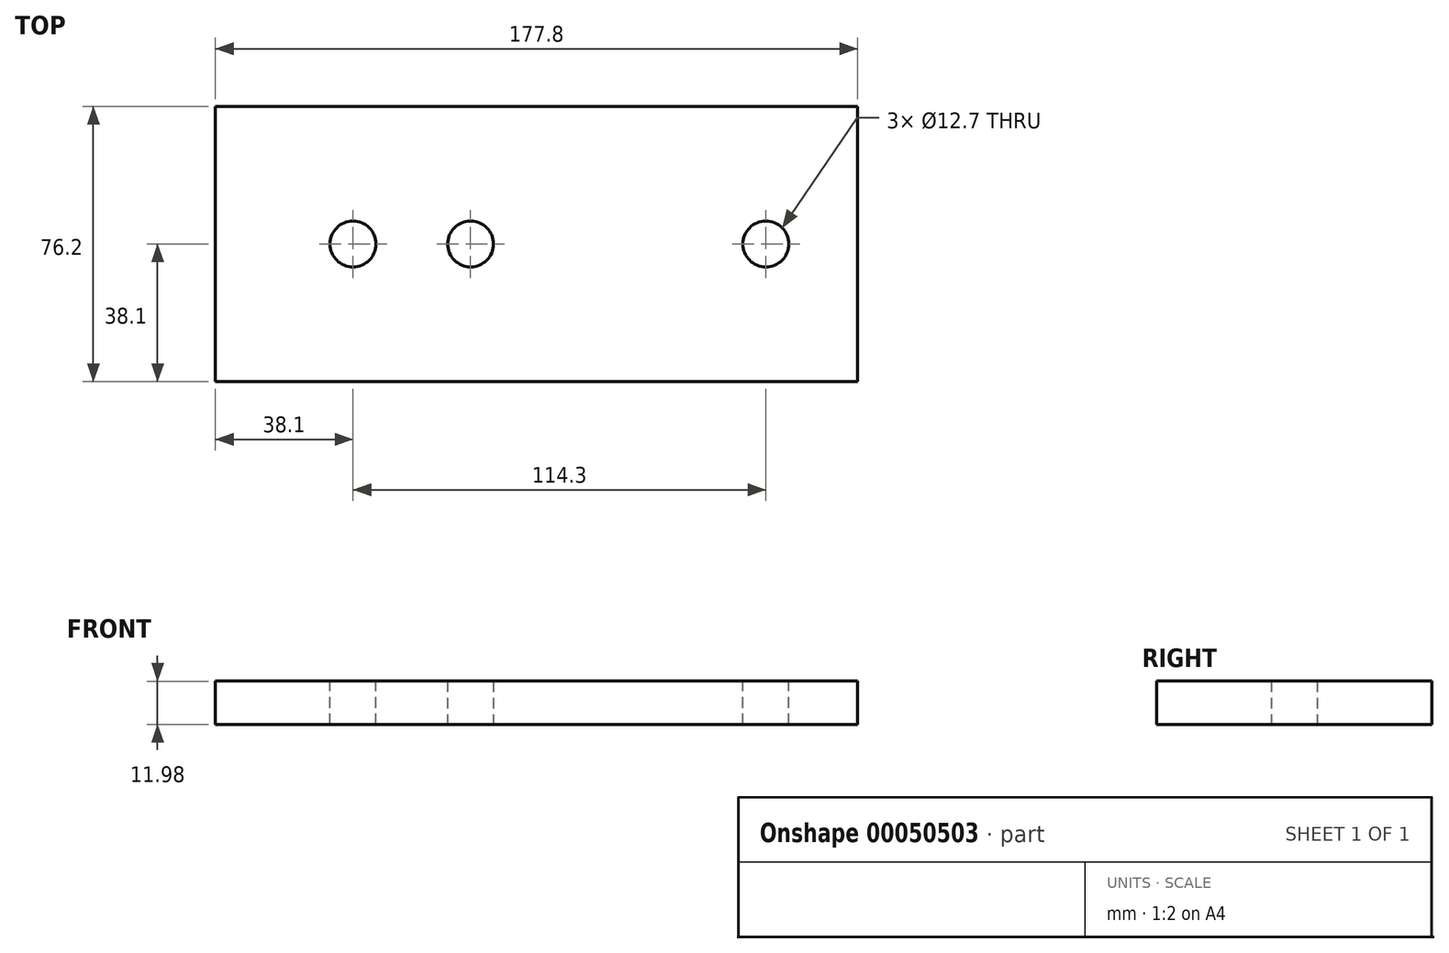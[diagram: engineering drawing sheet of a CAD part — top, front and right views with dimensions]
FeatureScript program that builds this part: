
annotation { "Feature Type Name" : "Feature", "Feature Type Description" : "" }
export const myFeature = defineFeature(function(context is Context, id is Id, definition is map)
    precondition{}
    {
        {
            var Q0;
            Q0=qCreatedBy(makeId("Top.planeOp"),FACE);
            var sketch = newSketch(context, id + "F0", { "sketchPlane" : qUnion([Q0])});
            skLineSegment(sketch, "E0.rect.bottom", {"start": v(387.35, 38.1) * mm, "end": v(-387.35, 38.1) * mm});
            skLineSegment(sketch, "E0.rect.top", {"start": v(387.35, -38.1) * mm, "end": v(-387.35, -38.1) * mm});
            skLineSegment(sketch, "E0.rect.left", {"start": v(387.35, 38.1) * mm, "end": v(387.35, -38.1) * mm});
            skLineSegment(sketch, "E0.rect.right", {"start": v(-387.35, 38.1) * mm, "end": v(-387.35, -38.1) * mm});
            skPoint(sketch, "E0.rect.middle", {"position": v(0, 0) * mm});
            skSolve(sketch);
        }
        {
            var Q0;
            Q0 = qSketchRegion(id + "F0", true);
            extrude(context, id + "F1", {"entities" : qUnion([Q0]), "endBound" : BoundingType.SYMMETRIC, "depth" : 12 * mm});
        }
        {
            var Q0;
            Q0=makeQuery(id+"F1.opExtrude","CAP_FACE",FACE,{"disambiguationData":[OSD([sQuery(id+"F0.wireOp",EDGE,"E0.rect.bottom"),sQuery(id+"F0.wireOp",EDGE,"E0.rect.top"),sQuery(id+"F0.wireOp",EDGE,"E0.rect.left"),sQuery(id+"F0.wireOp",EDGE,"E0.rect.right")])],"isStart":true});
            var sketch = newSketch(context, id + "F2", { "sketchPlane" : qUnion([Q0])});
            skCircle(sketch, "E1", {"center": v(-316.7, 0) * mm, "radius": 6.35 * mm});
            skCircle(sketch, "E2", {"center": v(323.85, 0) * mm, "radius": 6.35 * mm});
            skSolve(sketch);
        }
        {
            var Q0;
            Q0 = qSketchRegion(id + "F2", true);
            extrude(context, id + "F3", {"entities" : qUnion([Q0]), "operationType" : NewBodyOperationType.REMOVE, "endBound" : BoundingType.UP_TO_NEXT, "oppositeDirection" : true, "depth" : 25.4 * mm});
        }
        {
            var Q0;
            Q0=makeQuery(id+"F1.opExtrude","CAP_FACE",FACE,{"disambiguationData":[OSD([sQuery(id+"F0.wireOp",EDGE,"E0.rect.bottom"),sQuery(id+"F0.wireOp",EDGE,"E0.rect.top"),sQuery(id+"F0.wireOp",EDGE,"E0.rect.left"),sQuery(id+"F0.wireOp",EDGE,"E0.rect.right")])],"isStart":false});
            var sketch = newSketch(context, id + "F4", { "sketchPlane" : qUnion([Q0])});
            skLineSegment(sketch, "E3.bottom", {"start": v(-349.25, 0) * mm, "end": v(-234.95, 0) * mm, "construction": true});
            skCircle(sketch, "E4", {"center": v(-349.25, 0) * mm, "radius": 6.35 * mm});
            skCircle(sketch, "E5", {"center": v(-234.95, 0) * mm, "radius": 6.35 * mm});
            skLineSegment(sketch, "E6", {"start": v(-316.7, 0) * mm, "end": v(-292.1, 0) * mm, "construction": true});
            skSolve(sketch);
        }
        {
            var Q0;
            Q0 = qSketchRegion(id + "F4", true);
            extrude(context, id + "F5", {"entities" : qUnion([Q0]), "operationType" : NewBodyOperationType.REMOVE, "endBound" : BoundingType.UP_TO_NEXT, "oppositeDirection" : true, "depth" : 25.4 * mm});
        }
        {
            var Q0;
            Q0=makeQuery(id+"F1.opExtrude","CAP_FACE",FACE,{"disambiguationData":[OSD([sQuery(id+"F0.wireOp",EDGE,"E0.rect.bottom"),sQuery(id+"F0.wireOp",EDGE,"E0.rect.top"),sQuery(id+"F0.wireOp",EDGE,"E0.rect.left"),sQuery(id+"F0.wireOp",EDGE,"E0.rect.right")])],"isStart":false});
            var sketch = newSketch(context, id + "F6", { "sketchPlane" : qUnion([Q0])});
            skLineSegment(sketch, "E7.bottom", {"start": v(-209.55, 38.1) * mm, "end": v(387.35, 38.1) * mm});
            skLineSegment(sketch, "E7.top", {"start": v(-209.55, -38.1) * mm, "end": v(387.35, -38.1) * mm});
            skLineSegment(sketch, "E7.left", {"start": v(-209.55, 38.1) * mm, "end": v(-209.55, -38.1) * mm});
            skLineSegment(sketch, "E7.right", {"start": v(387.35, 38.1) * mm, "end": v(387.35, -38.1) * mm});
            skSolve(sketch);
        }
        {
            var Q0;
            Q0 = qSketchRegion(id + "F6", true);
            extrude(context, id + "F7", {"entities" : qUnion([Q0]), "operationType" : NewBodyOperationType.REMOVE, "endBound" : BoundingType.UP_TO_NEXT, "oppositeDirection" : true, "depth" : 25.4 * mm});
        }
    });
